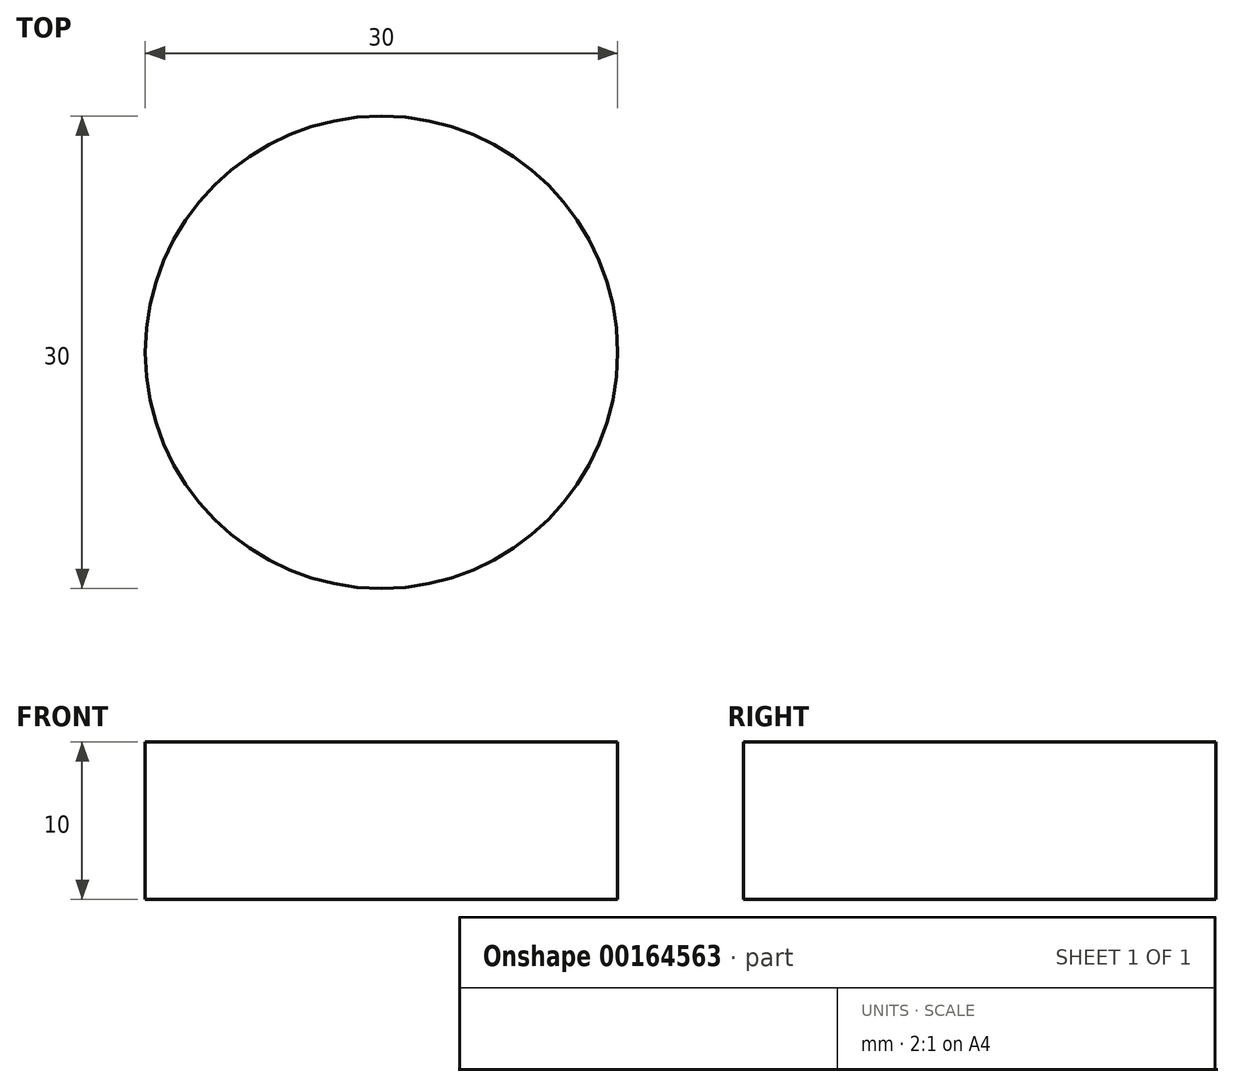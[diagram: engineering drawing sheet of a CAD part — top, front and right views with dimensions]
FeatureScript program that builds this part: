
annotation { "Feature Type Name" : "Feature", "Feature Type Description" : "" }
export const myFeature = defineFeature(function(context is Context, id is Id, definition is map)
    precondition{}
    {
        {
            var Q0;
            Q0=qCreatedBy(makeId("Top.planeOp"),FACE);
            var sketch = newSketch(context, id + "F0", { "sketchPlane" : qUnion([Q0])});
            skCircle(sketch, "E0", {"center": v(0, 0) * mm, "radius": 15 * mm});
            skSolve(sketch);
        }
        {
            var Q0;
            Q0=makeQuery(id+"F0.imprint","IMPRINT",FACE,{"disambiguationData":[TD([[makeQuery(id+"F0.imprint","IMPRINT",EDGE,{"derivedFrom":sQuery(id+"F0.wireOp",EDGE,"E0")}),1.0]])]});
            extrude(context, id + "F1", {"entities" : qUnion([Q0]), "depth" : 10 * mm});
        }
    });
